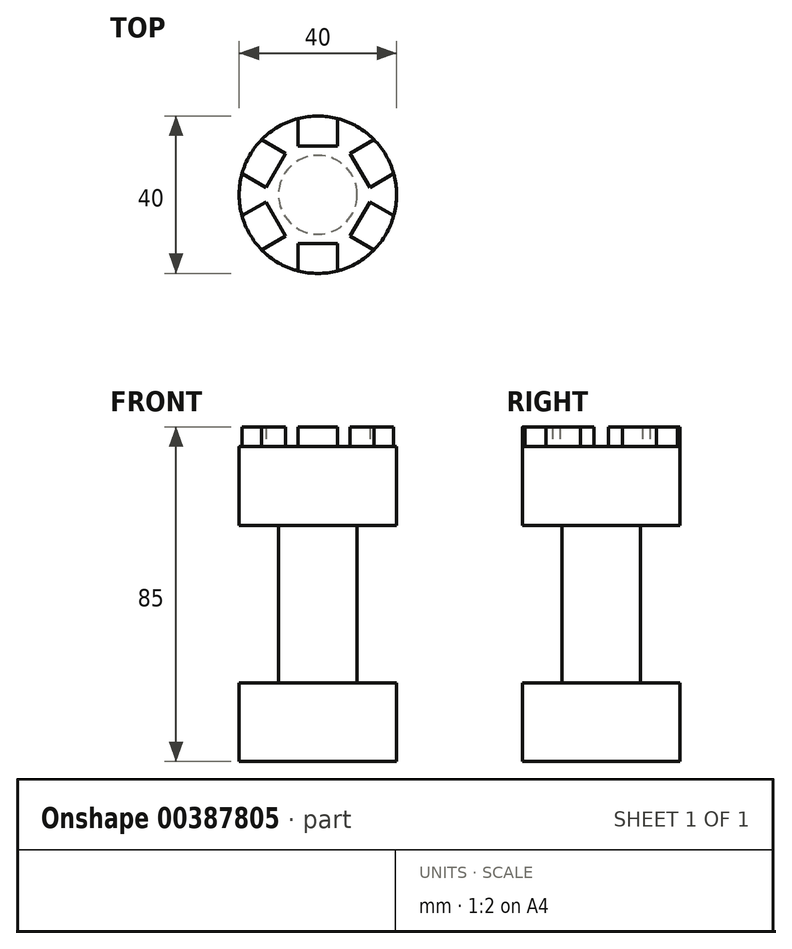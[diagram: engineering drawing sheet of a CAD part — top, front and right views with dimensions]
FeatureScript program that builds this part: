
annotation { "Feature Type Name" : "Feature", "Feature Type Description" : "" }
export const myFeature = defineFeature(function(context is Context, id is Id, definition is map)
    precondition{}
    {
        {
            var Q0;
            Q0=qCreatedBy(makeId("Front.planeOp"),FACE);
            var sketch = newSketch(context, id + "F0", { "sketchPlane" : qUnion([Q0])});
            skLineSegment(sketch, "E0", {"start": v(0, 68.86) * mm, "end": v(0, -63.55) * mm, "construction": true});
            skLineSegment(sketch, "E1", {"start": v(0, 40) * mm, "end": v(0, -40) * mm});
            skLineSegment(sketch, "E2", {"start": v(0, -40) * mm, "end": v(20, -40) * mm});
            skLineSegment(sketch, "E3", {"start": v(20, -40) * mm, "end": v(20, -20) * mm});
            skLineSegment(sketch, "E4", {"start": v(20, -20) * mm, "end": v(10, -20) * mm});
            skLineSegment(sketch, "E5", {"start": v(10, -20) * mm, "end": v(10, 20) * mm});
            skLineSegment(sketch, "E6", {"start": v(10, 20) * mm, "end": v(20, 20) * mm});
            skLineSegment(sketch, "E7", {"start": v(20, 20) * mm, "end": v(20, 40) * mm});
            skLineSegment(sketch, "E8", {"start": v(20, 40) * mm, "end": v(0, 40) * mm});
            skSolve(sketch);
        }
        {
            var Q0;
            Q0=makeQuery(id+"F0.imprint","IMPRINT",FACE,{"disambiguationData":[TD([[makeQuery(id+"F0.imprint","IMPRINT",EDGE,{"derivedFrom":sQuery(id+"F0.wireOp",EDGE,"E1")}),1.0]])]});
            var Q1;
            Q1=sQuery(id+"F0.wireOp",EDGE,"E0");
            revolve(context, id + "F1", {"entities" : qUnion([Q0]), "axis" : qUnion([Q1]), "revolveType" : RevolveType.FULL});
        }
        {
            var Q0;
            Q0=makeQuery(id+"F1.opRevolve","SWEPT_FACE",FACE,{"disambiguationData":[OSD([sQuery(id+"F0.wireOp",EDGE,"E8")])]});
            var sketch = newSketch(context, id + "F2", { "sketchPlane" : qUnion([Q0])});
            skLineSegment(sketch, "E9", {"start": v(-5, 19.36) * mm, "end": v(-5, 12.36) * mm});
            skLineSegment(sketch, "E10", {"start": v(-5, 12.36) * mm, "end": v(5, 12.36) * mm});
            skLineSegment(sketch, "E11", {"start": v(5, 12.36) * mm, "end": v(5, 19.36) * mm});
            skCircle(sketch, "E12", {"center": v(0, 0) * mm, "radius": 20 * mm});
            skArc(sketch, "E13", {"start": v(5, 19.36) * mm, "mid": v(0, 20) * mm, "end": v(-5, 19.36) * mm});
            skSolve(sketch);
        }
        {
            var Q0;
            {var subQ0=sQuery(id+"F2.wireOp",EDGE,"E9");Q0=makeQuery(id+"F2.imprint","IMPRINT",FACE,{"disambiguationData":[TD([[makeQuery(id+"F2.imprint","IMPRINT",EDGE,{"derivedFrom":subQ0}),1.0]])]});}
            extrude(context, id + "F3", {"entities" : qUnion([Q0]), "operationType" : NewBodyOperationType.ADD, "depth" : 5 * mm});
        }
        {
            var Q0;
            Q0=makeQuery(id+"F1.opRevolve","SWEPT_BODY",BODY,{"disambiguationData":[OSD([sQuery(id+"F0.wireOp",EDGE,"E1"),sQuery(id+"F0.wireOp",EDGE,"E2"),sQuery(id+"F0.wireOp",EDGE,"E3"),sQuery(id+"F0.wireOp",EDGE,"E4"),sQuery(id+"F0.wireOp",EDGE,"E5"),sQuery(id+"F0.wireOp",EDGE,"E6"),sQuery(id+"F0.wireOp",EDGE,"E7"),sQuery(id+"F0.wireOp",EDGE,"E8")])]});
            var Q1;
            Q1=makeQuery(id+"F3.boolean.opBoolean","MERGE",FACE,{"derivedFrom":[makeQuery(id+"F1.opRevolve","SWEPT_FACE",FACE,{"disambiguationData":[OSD([sQuery(id+"F0.wireOp",EDGE,"E7")])]}),makeQuery(id+"F3.opExtrude","SWEPT_FACE",FACE,{"disambiguationData":[OSD([sQuery(id+"F2.wireOp",EDGE,"E12")])]})]});
            circularPattern(context, id + "F4", {"entities" : qUnion([Q0]), "axis" : qUnion([Q1]), "angle" : 360 * degree, "instanceCount" : 6, "equalSpace" : true});
        }
    });
